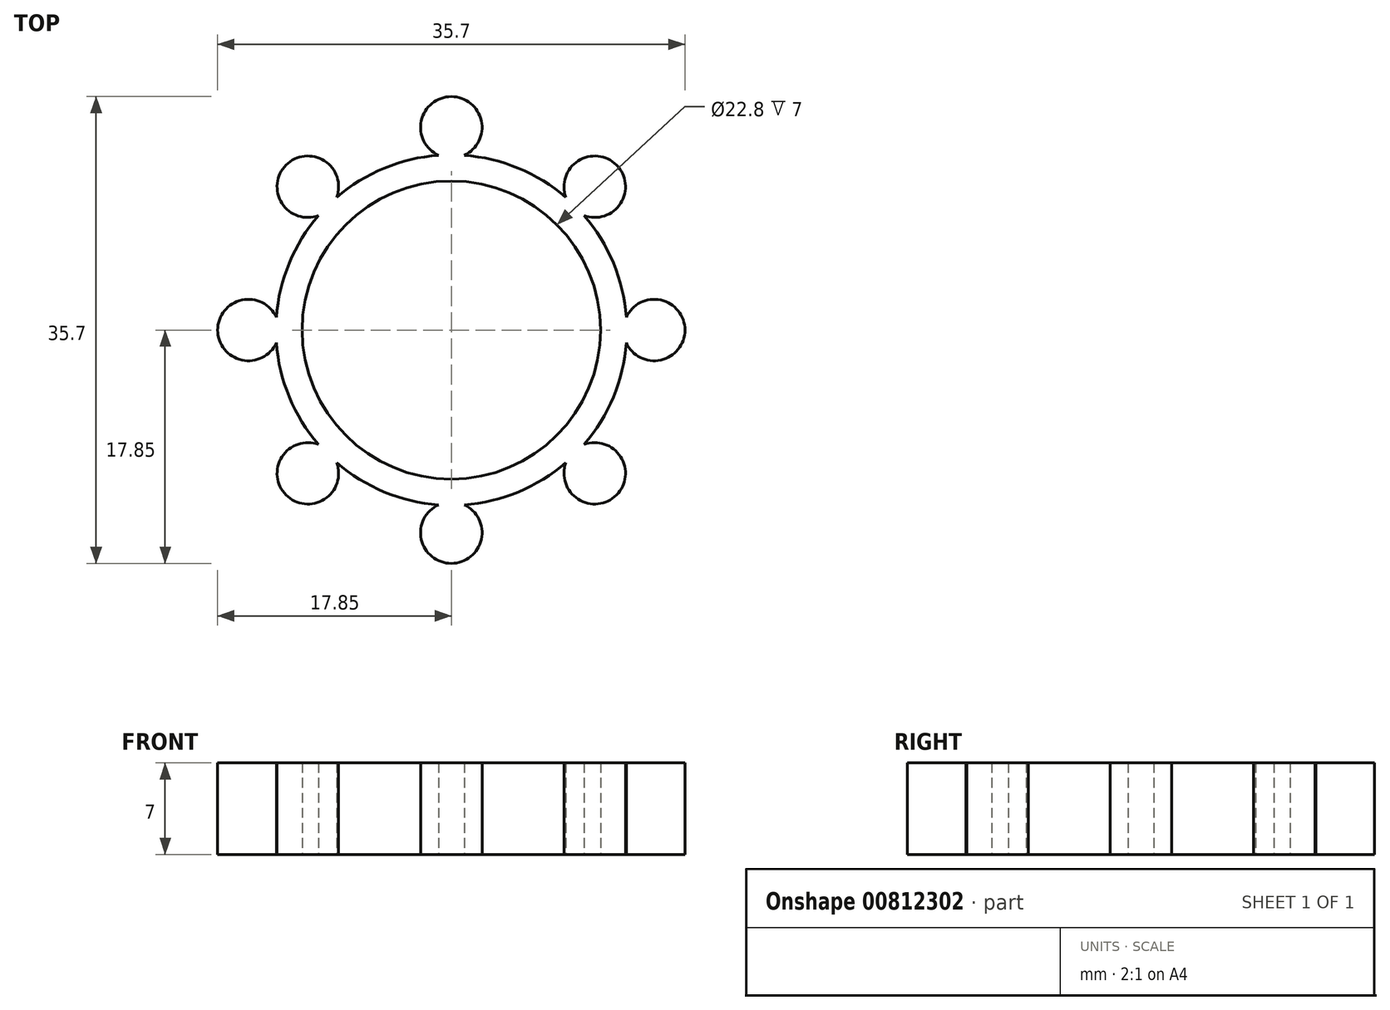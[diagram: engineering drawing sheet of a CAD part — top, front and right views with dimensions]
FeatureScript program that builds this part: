
annotation { "Feature Type Name" : "Feature", "Feature Type Description" : "" }
export const myFeature = defineFeature(function(context is Context, id is Id, definition is map)
    precondition{}
    {
        {
            var Q0;
            Q0=qCreatedBy(makeId("Top.planeOp"),FACE);
            var sketch = newSketch(context, id + "F0", { "sketchPlane" : qUnion([Q0])});
            skCircle(sketch, "E0", {"center": v(0, 0) * mm, "radius": 11.4 * mm});
            skCircle(sketch, "E1", {"center": v(0, 0) * mm, "radius": 13.4 * mm});
            skLineSegment(sketch, "E2", {"start": v(0, 0) * mm, "end": v(0, 26.16) * mm, "construction": true});
            skCircle(sketch, "E3", {"center": v(0, 15.5) * mm, "radius": 2.35 * mm});
            skCircle(sketch, "E4.1.0", {"center": v(-10.96, 10.96) * mm, "radius": 2.35 * mm});
            skCircle(sketch, "E4.2.0", {"center": v(-15.5, 0) * mm, "radius": 2.35 * mm});
            skCircle(sketch, "E4.3.0", {"center": v(-10.96, -10.96) * mm, "radius": 2.35 * mm});
            skCircle(sketch, "E4.4.0", {"center": v(0, -15.5) * mm, "radius": 2.35 * mm});
            skCircle(sketch, "E4.5.0", {"center": v(10.96, -10.96) * mm, "radius": 2.35 * mm});
            skCircle(sketch, "E4.6.0", {"center": v(15.5, 0) * mm, "radius": 2.35 * mm});
            skCircle(sketch, "E4.7.0", {"center": v(10.96, 10.96) * mm, "radius": 2.35 * mm});
            skSolve(sketch);
        }
        {
            var Q0;
            Q0=makeQuery(id+"F0.imprint","IMPRINT",FACE,{"disambiguationData":[TD([[makeQuery(id+"F0.imprint","IMPRINT",EDGE,{"derivedFrom":sQuery(id+"F0.wireOp",EDGE,"E0")}),-1.0]])]});
            var Q1;
            {var subQ0=sQuery(id+"F0.wireOp",EDGE,"E4.1.0");var subQ1=sQuery(id+"F0.wireOp",EDGE,"E1");var subQ2=makeQuery(id+"F0.imprint","INTERSECT",VERTEX,{"disambiguationData":[OD(0.0)],"derivedFrom":[subQ1,subQ0]});Q1=makeQuery(id+"F0.imprint","IMPRINT",FACE,{"disambiguationData":[TD([[makeQuery(id+"F0.imprint","IMPRINT",EDGE,{"disambiguationData":[TD([[subQ2,-1.0]])],"derivedFrom":subQ1}),-1.0]])]});}
            var Q2;
            {var subQ0=sQuery(id+"F0.wireOp",EDGE,"E3");var subQ1=sQuery(id+"F0.wireOp",EDGE,"E1");var subQ2=makeQuery(id+"F0.imprint","INTERSECT",VERTEX,{"disambiguationData":[OD(0.0)],"derivedFrom":[subQ1,subQ0]});Q2=makeQuery(id+"F0.imprint","IMPRINT",FACE,{"disambiguationData":[TD([[makeQuery(id+"F0.imprint","IMPRINT",EDGE,{"disambiguationData":[TD([[subQ2,-1.0]])],"derivedFrom":subQ1}),-1.0]])]});}
            var Q3;
            {var subQ0=sQuery(id+"F0.wireOp",EDGE,"E4.7.0");var subQ1=sQuery(id+"F0.wireOp",EDGE,"E1");var subQ2=makeQuery(id+"F0.imprint","INTERSECT",VERTEX,{"disambiguationData":[OD(0.0)],"derivedFrom":[subQ1,subQ0]});Q3=makeQuery(id+"F0.imprint","IMPRINT",FACE,{"disambiguationData":[TD([[makeQuery(id+"F0.imprint","IMPRINT",EDGE,{"disambiguationData":[TD([[subQ2,-1.0]])],"derivedFrom":subQ1}),-1.0]])]});}
            var Q4;
            {var subQ0=sQuery(id+"F0.wireOp",EDGE,"E4.6.0");var subQ1=sQuery(id+"F0.wireOp",EDGE,"E1");var subQ2=makeQuery(id+"F0.imprint","INTERSECT",VERTEX,{"disambiguationData":[OD(0.0)],"derivedFrom":[subQ1,subQ0]});Q4=makeQuery(id+"F0.imprint","IMPRINT",FACE,{"disambiguationData":[TD([[makeQuery(id+"F0.imprint","IMPRINT",EDGE,{"disambiguationData":[TD([[subQ2,1.0]])],"derivedFrom":subQ1}),-1.0]])]});}
            var Q5;
            {var subQ0=sQuery(id+"F0.wireOp",EDGE,"E4.5.0");var subQ1=sQuery(id+"F0.wireOp",EDGE,"E1");var subQ2=makeQuery(id+"F0.imprint","INTERSECT",VERTEX,{"disambiguationData":[OD(0.0)],"derivedFrom":[subQ1,subQ0]});Q5=makeQuery(id+"F0.imprint","IMPRINT",FACE,{"disambiguationData":[TD([[makeQuery(id+"F0.imprint","IMPRINT",EDGE,{"disambiguationData":[TD([[subQ2,-1.0]])],"derivedFrom":subQ1}),-1.0]])]});}
            var Q6;
            {var subQ0=sQuery(id+"F0.wireOp",EDGE,"E4.4.0");var subQ1=sQuery(id+"F0.wireOp",EDGE,"E1");var subQ2=makeQuery(id+"F0.imprint","INTERSECT",VERTEX,{"disambiguationData":[OD(0.0)],"derivedFrom":[subQ1,subQ0]});Q6=makeQuery(id+"F0.imprint","IMPRINT",FACE,{"disambiguationData":[TD([[makeQuery(id+"F0.imprint","IMPRINT",EDGE,{"disambiguationData":[TD([[subQ2,-1.0]])],"derivedFrom":subQ1}),-1.0]])]});}
            var Q7;
            {var subQ0=sQuery(id+"F0.wireOp",EDGE,"E4.3.0");var subQ1=sQuery(id+"F0.wireOp",EDGE,"E1");var subQ2=makeQuery(id+"F0.imprint","INTERSECT",VERTEX,{"disambiguationData":[OD(0.0)],"derivedFrom":[subQ1,subQ0]});Q7=makeQuery(id+"F0.imprint","IMPRINT",FACE,{"disambiguationData":[TD([[makeQuery(id+"F0.imprint","IMPRINT",EDGE,{"disambiguationData":[TD([[subQ2,-1.0]])],"derivedFrom":subQ1}),-1.0]])]});}
            var Q8;
            {var subQ0=sQuery(id+"F0.wireOp",EDGE,"E4.2.0");var subQ1=sQuery(id+"F0.wireOp",EDGE,"E1");var subQ2=makeQuery(id+"F0.imprint","INTERSECT",VERTEX,{"disambiguationData":[OD(0.0)],"derivedFrom":[subQ1,subQ0]});Q8=makeQuery(id+"F0.imprint","IMPRINT",FACE,{"disambiguationData":[TD([[makeQuery(id+"F0.imprint","IMPRINT",EDGE,{"disambiguationData":[TD([[subQ2,-1.0]])],"derivedFrom":subQ1}),-1.0]])]});}
            var Q9;
            {var subQ0=sQuery(id+"F0.wireOp",EDGE,"E4.2.0");var subQ1=sQuery(id+"F0.wireOp",EDGE,"E1");var subQ2=makeQuery(id+"F0.imprint","INTERSECT",VERTEX,{"disambiguationData":[OD(0.0)],"derivedFrom":[subQ1,subQ0]});Q9=makeQuery(id+"F0.imprint","IMPRINT",FACE,{"disambiguationData":[TD([[makeQuery(id+"F0.imprint","IMPRINT",EDGE,{"disambiguationData":[TD([[subQ2,-1.0]])],"derivedFrom":subQ1}),1.0]])]});}
            var Q10;
            {var subQ0=sQuery(id+"F0.wireOp",EDGE,"E4.3.0");var subQ1=sQuery(id+"F0.wireOp",EDGE,"E1");var subQ2=makeQuery(id+"F0.imprint","INTERSECT",VERTEX,{"disambiguationData":[OD(0.0)],"derivedFrom":[subQ1,subQ0]});Q10=makeQuery(id+"F0.imprint","IMPRINT",FACE,{"disambiguationData":[TD([[makeQuery(id+"F0.imprint","IMPRINT",EDGE,{"disambiguationData":[TD([[subQ2,-1.0]])],"derivedFrom":subQ1}),1.0]])]});}
            var Q11;
            {var subQ0=sQuery(id+"F0.wireOp",EDGE,"E4.5.0");var subQ1=sQuery(id+"F0.wireOp",EDGE,"E1");var subQ2=makeQuery(id+"F0.imprint","INTERSECT",VERTEX,{"disambiguationData":[OD(0.0)],"derivedFrom":[subQ1,subQ0]});Q11=makeQuery(id+"F0.imprint","IMPRINT",FACE,{"disambiguationData":[TD([[makeQuery(id+"F0.imprint","IMPRINT",EDGE,{"disambiguationData":[TD([[subQ2,-1.0]])],"derivedFrom":subQ1}),1.0]])]});}
            var Q12;
            {var subQ0=sQuery(id+"F0.wireOp",EDGE,"E4.6.0");var subQ1=sQuery(id+"F0.wireOp",EDGE,"E1");var subQ2=makeQuery(id+"F0.imprint","INTERSECT",VERTEX,{"disambiguationData":[OD(0.0)],"derivedFrom":[subQ1,subQ0]});Q12=makeQuery(id+"F0.imprint","IMPRINT",FACE,{"disambiguationData":[TD([[makeQuery(id+"F0.imprint","IMPRINT",EDGE,{"disambiguationData":[TD([[subQ2,1.0]])],"derivedFrom":subQ1}),1.0]])]});}
            var Q13;
            {var subQ0=sQuery(id+"F0.wireOp",EDGE,"E4.4.0");var subQ1=sQuery(id+"F0.wireOp",EDGE,"E1");var subQ2=makeQuery(id+"F0.imprint","INTERSECT",VERTEX,{"disambiguationData":[OD(0.0)],"derivedFrom":[subQ1,subQ0]});Q13=makeQuery(id+"F0.imprint","IMPRINT",FACE,{"disambiguationData":[TD([[makeQuery(id+"F0.imprint","IMPRINT",EDGE,{"disambiguationData":[TD([[subQ2,-1.0]])],"derivedFrom":subQ1}),1.0]])]});}
            var Q14;
            {var subQ0=sQuery(id+"F0.wireOp",EDGE,"E4.7.0");var subQ1=sQuery(id+"F0.wireOp",EDGE,"E1");var subQ2=makeQuery(id+"F0.imprint","INTERSECT",VERTEX,{"disambiguationData":[OD(0.0)],"derivedFrom":[subQ1,subQ0]});Q14=makeQuery(id+"F0.imprint","IMPRINT",FACE,{"disambiguationData":[TD([[makeQuery(id+"F0.imprint","IMPRINT",EDGE,{"disambiguationData":[TD([[subQ2,-1.0]])],"derivedFrom":subQ1}),1.0]])]});}
            var Q15;
            {var subQ0=sQuery(id+"F0.wireOp",EDGE,"E3");var subQ1=sQuery(id+"F0.wireOp",EDGE,"E1");var subQ2=makeQuery(id+"F0.imprint","INTERSECT",VERTEX,{"disambiguationData":[OD(0.0)],"derivedFrom":[subQ1,subQ0]});Q15=makeQuery(id+"F0.imprint","IMPRINT",FACE,{"disambiguationData":[TD([[makeQuery(id+"F0.imprint","IMPRINT",EDGE,{"disambiguationData":[TD([[subQ2,-1.0]])],"derivedFrom":subQ1}),1.0]])]});}
            var Q16;
            {var subQ0=sQuery(id+"F0.wireOp",EDGE,"E4.1.0");var subQ1=sQuery(id+"F0.wireOp",EDGE,"E1");var subQ2=makeQuery(id+"F0.imprint","INTERSECT",VERTEX,{"disambiguationData":[OD(0.0)],"derivedFrom":[subQ1,subQ0]});Q16=makeQuery(id+"F0.imprint","IMPRINT",FACE,{"disambiguationData":[TD([[makeQuery(id+"F0.imprint","IMPRINT",EDGE,{"disambiguationData":[TD([[subQ2,-1.0]])],"derivedFrom":subQ1}),1.0]])]});}
            extrude(context, id + "F1", {"entities" : qUnion([Q0, Q1, Q2, Q3, Q4, Q5, Q6, Q7, Q8, Q9, Q10, Q11, Q12, Q13, Q14, Q15, Q16]), "depth" : 7 * mm, "offsetDistance" : 25 * mm});
        }
    });
